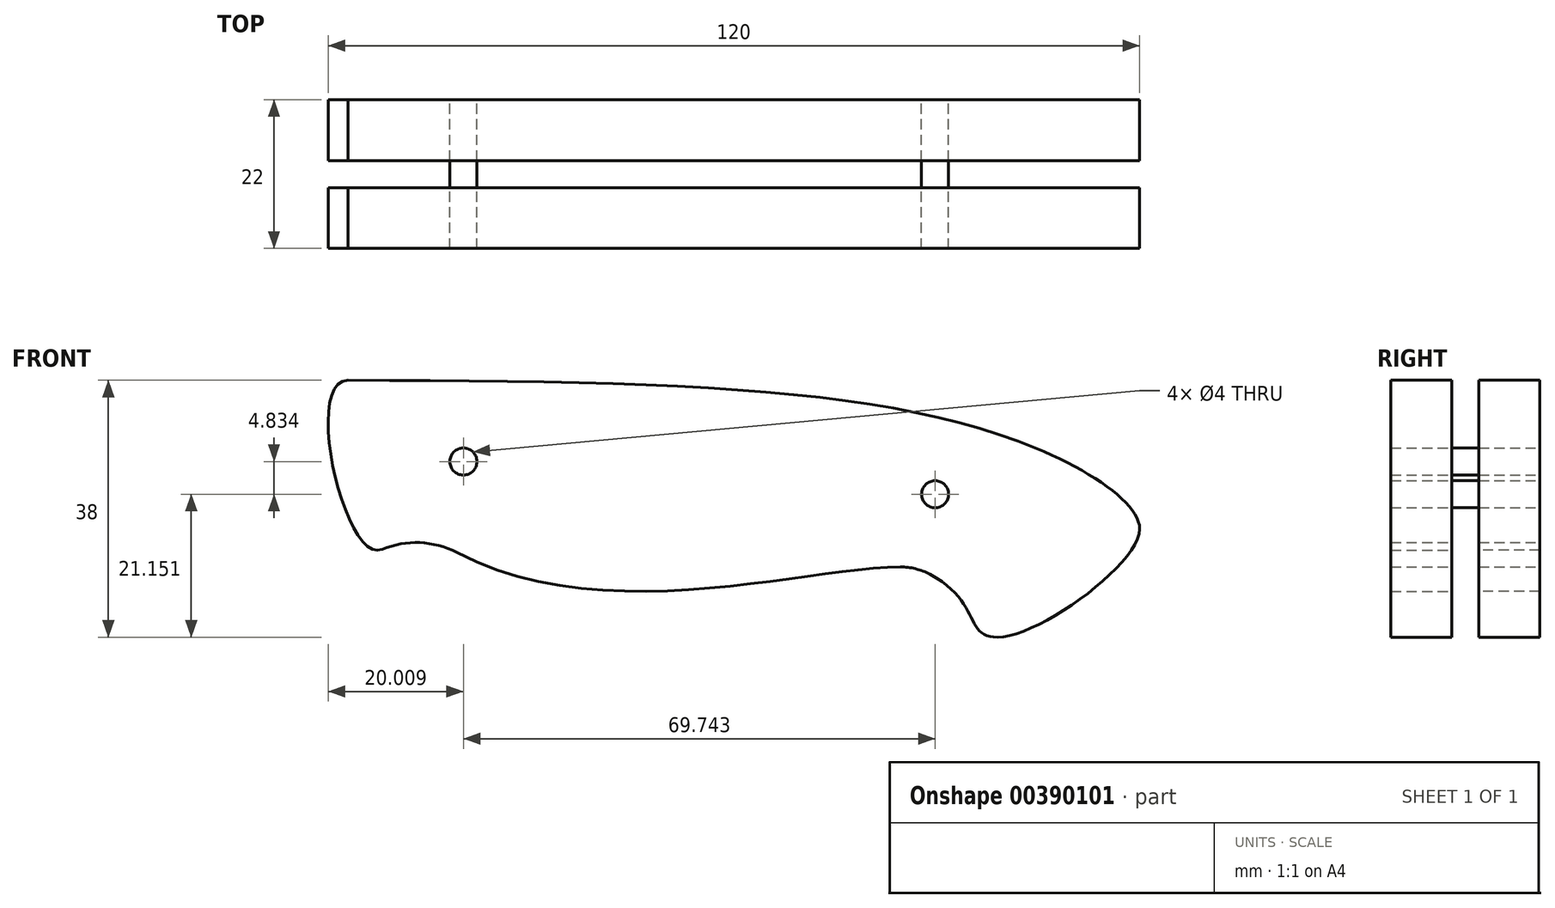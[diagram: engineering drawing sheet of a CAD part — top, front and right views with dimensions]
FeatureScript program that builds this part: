
annotation { "Feature Type Name" : "Feature", "Feature Type Description" : "" }
export const myFeature = defineFeature(function(context is Context, id is Id, definition is map)
    precondition{}
    {
        {
            var Q0;
            Q0=qCreatedBy(makeId("Front.planeOp"),FACE);
            var sketch = newSketch(context, id + "F0", { "sketchPlane" : qUnion([Q0])});
            skLineSegment(sketch, "E0.bottom", {"start": v(0, 0) * mm, "end": v(230, 0) * mm});
            skLineSegment(sketch, "E0.top", {"start": v(0, -38) * mm, "end": v(230, -38) * mm});
            skLineSegment(sketch, "E0.left", {"start": v(0, 0) * mm, "end": v(0, -38) * mm});
            skLineSegment(sketch, "E0.right", {"start": v(230, 0) * mm, "end": v(230, -38) * mm});
            skSolve(sketch);
        }
        {
            var Q0;
            Q0=makeQuery(id+"F0.imprint","IMPRINT",FACE,{"disambiguationData":[TD([[makeQuery(id+"F0.imprint","IMPRINT",EDGE,{"derivedFrom":sQuery(id+"F0.wireOp",EDGE,"E0.bottom")}),-1.0]])]});
            var sketch = newSketch(context, id + "F1", { "sketchPlane" : qUnion([Q0])});
            skLineSegment(sketch, "E1", {"start": v(0, 0) * mm, "end": v(0, -10) * mm, "construction": true});
            skLineSegment(sketch, "E2", {"start": v(110, 0) * mm, "end": v(230, 0) * mm, "construction": true});
            skLineSegment(sketch, "E3", {"start": v(110, 0) * mm, "end": v(110, -38) * mm, "construction": true});
            skFitSpline(sketch, "E4", {"points": [v(0, -10) * mm, v(110, -38) * mm], "startDerivative": vector(51, -84) * mm, "endDerivative": vector(120, 0) * mm});
            skFitSpline(sketch, "E5", {"points": [v(0, -10) * mm, v(110, 0) * mm], "startDerivative": vector(150, 30) * mm, "endDerivative": vector(210, 0) * mm});
            skLineSegment(sketch, "E6", {"start": v(110, -38) * mm, "end": v(70, -38) * mm, "construction": true});
            skLineSegment(sketch, "E7", {"start": v(110, 0) * mm, "end": v(40, 0) * mm, "construction": true});
            skLineSegment(sketch, "E8", {"start": v(110, 0) * mm, "end": v(0, 0) * mm, "construction": true});
            skLineSegment(sketch, "E9", {"start": v(110, -38) * mm, "end": v(123, -38) * mm, "construction": true});
            skLineSegment(sketch, "E10", {"start": v(123, -38) * mm, "end": v(123, -37) * mm, "construction": true});
            skArc(sketch, "E11", {"start": v(129, -25.47) * mm, "mid": v(116.25, -25.89) * mm, "end": v(110, -37) * mm});
            skFitSpline(sketch, "E12", {"points": [v(110, 0) * mm, v(212, -9) * mm, v(230, -22) * mm], "startDerivative": vector(219.85, 0) * mm, "endDerivative": vector(0, -37.77) * mm});
            skLineSegment(sketch, "E13", {"start": v(230, 0) * mm, "end": v(230, -22) * mm, "construction": true});
            skLineSegment(sketch, "E14", {"start": v(110, 0) * mm, "end": v(160, 0) * mm, "construction": true});
            skLineSegment(sketch, "E15", {"start": v(230, -22) * mm, "end": v(230, -18) * mm, "construction": true});
            skLineSegment(sketch, "E16", {"start": v(230, -38) * mm, "end": v(209, -38) * mm, "construction": true});
            skFitSpline(sketch, "E17", {"points": [v(230, -22) * mm, v(209, -38) * mm], "startDerivative": vector(0, -15.6) * mm, "endDerivative": vector(-18, 0) * mm});
            skLineSegment(sketch, "E18", {"start": v(230, -22) * mm, "end": v(230, -27.2) * mm, "construction": true});
            skLineSegment(sketch, "E19", {"start": v(209, -38) * mm, "end": v(215, -38) * mm, "construction": true});
            skLineSegment(sketch, "E20", {"start": v(129, -25.47) * mm, "end": v(151.18, -37) * mm, "construction": true});
            skArc(sketch, "E21", {"start": v(199, -28.7) * mm, "mid": v(196.87, -27.88) * mm, "end": v(194.6, -27.6) * mm});
            skLineSegment(sketch, "E22", {"start": v(194.6, -27.6) * mm, "end": v(180.6, -27.6) * mm, "construction": true});
            skFitSpline(sketch, "E23", {"points": [v(129, -25.47) * mm, v(194.6, -27.6) * mm], "startDerivative": vector(66.53, -34.62) * mm, "endDerivative": vector(42, 0) * mm});
            skLineSegment(sketch, "E24", {"start": v(204, -38) * mm, "end": v(209, -38) * mm, "construction": true});
            skLineSegment(sketch, "E25", {"start": v(194.6, -37) * mm, "end": v(204, -37) * mm, "construction": true});
            skLineSegment(sketch, "E26", {"start": v(199, -28.7) * mm, "end": v(206.6, -32.72) * mm, "construction": true});
            skFitSpline(sketch, "E27", {"points": [v(199, -28.7) * mm, v(209, -38) * mm], "startDerivative": vector(22.8, -12.08) * mm, "endDerivative": vector(15, 0) * mm});
            skLineSegment(sketch, "E28", {"start": v(209, -38) * mm, "end": v(204, -38) * mm, "construction": true});
            skLineSegment(sketch, "E29", {"start": v(0, -38) * mm, "end": v(17, -38) * mm, "construction": true});
            skLineSegment(sketch, "E30", {"start": v(0, 0) * mm, "end": v(50, 0) * mm});
            skLineSegment(sketch, "E31", {"start": v(110, -25.47) * mm, "end": v(129, -25.47) * mm, "construction": true});
            skLineSegment(sketch, "E32", {"start": v(194.6, -27.6) * mm, "end": v(230, -27.6) * mm, "construction": true});
            skLineSegment(sketch, "E33", {"start": v(204, -38) * mm, "end": v(204, -37) * mm, "construction": true});
            skLineSegment(sketch, "E34", {"start": v(110, -38) * mm, "end": v(106, -38) * mm, "construction": true});
            skLineSegment(sketch, "E35", {"start": v(106, -38) * mm, "end": v(106, -10) * mm, "construction": true});
            skLineSegment(sketch, "E36", {"start": v(106, -10) * mm, "end": v(96, -10) * mm, "construction": true});
            skLineSegment(sketch, "E37", {"start": v(96, -10) * mm, "end": v(96, -20) * mm, "construction": true});
            skArc(sketch, "E38", {"start": v(106, -20) * mm, "mid": v(103.07, -12.93) * mm, "end": v(96, -10) * mm});
            skPoint(sketch, "E39", {"position": v(106, -20) * mm});
            skLineSegment(sketch, "E40", {"start": v(106, -20) * mm, "end": v(106, -38) * mm});
            skLineSegment(sketch, "E41", {"start": v(110, 0) * mm, "end": v(113, 0) * mm, "construction": true});
            skLineSegment(sketch, "E42", {"start": v(118, -25) * mm, "end": v(112.46, -27.3) * mm, "construction": true});
            skLineSegment(sketch, "E43", {"start": v(118, -25) * mm, "end": v(110, -25) * mm, "construction": true});
            skFitSpline(sketch, "E44", {"points": [v(113, 0) * mm, v(118, -25) * mm], "startDerivative": vector(-20.6, 0) * mm, "endDerivative": vector(16.62, 6.92) * mm});
            skLineSegment(sketch, "E45", {"start": v(96, -10) * mm, "end": v(96, 0) * mm});
            skLineSegment(sketch, "E46", {"start": v(110, -37) * mm, "end": v(110, -38) * mm});
            skLineSegment(sketch, "E47", {"start": v(110, -9) * mm, "end": v(212, -9) * mm, "construction": true});
            skLineSegment(sketch, "E48", {"start": v(212, 0) * mm, "end": v(212, -9) * mm});
            skLineSegment(sketch, "E49", {"start": v(199, -28.7) * mm, "end": v(230, -28.7) * mm, "construction": true});
            skFitSpline(sketch, "E50", {"points": [v(208, -7.62) * mm, v(214, -36.61) * mm], "startDerivative": vector(40.02, -12.74) * mm, "endDerivative": vector(-21.9, -9.84) * mm, "construction": true});
            skLineSegment(sketch, "E51", {"start": v(208, -7.62) * mm, "end": v(221.34, -11.87) * mm, "construction": true});
            skLineSegment(sketch, "E52", {"start": v(214, -36.61) * mm, "end": v(221.3, -33.33) * mm, "construction": true});
            skLineSegment(sketch, "E53", {"start": v(208, -7.62) * mm, "end": v(230, -7.62) * mm, "construction": true});
            skLineSegment(sketch, "E54", {"start": v(214, -36.61) * mm, "end": v(230, -36.61) * mm, "construction": true});
            skSolve(sketch);
        }
        {
            var Q0;
            Q0=makeQuery(id+"F0.imprint","IMPRINT",FACE,{"disambiguationData":[TD([[makeQuery(id+"F0.imprint","IMPRINT",EDGE,{"derivedFrom":sQuery(id+"F0.wireOp",EDGE,"E0.bottom")}),-1.0]])]});
            var sketch = newSketch(context, id + "F2", { "sketchPlane" : qUnion([Q0])});
            skLineSegment(sketch, "E55", {"start": v(123, -24) * mm, "end": v(123, 0) * mm, "construction": true});
            skLineSegment(sketch, "E56", {"start": v(198.06, -28.26) * mm, "end": v(206.44, -7.14) * mm, "construction": true});
            skFitSpline(sketch, "E57", {"points": [v(123, -12) * mm, v(202.25, -17.7) * mm], "startDerivative": vector(111, 0) * mm, "endDerivative": vector(34.3, -13.6) * mm, "construction": true});
            skLineSegment(sketch, "E58", {"start": v(202.25, -17.7) * mm, "end": v(190.82, -13.17) * mm, "construction": true});
            skCircle(sketch, "E59", {"center": v(130, -12.01) * mm, "radius": 2 * mm});
            skCircle(sketch, "E60", {"center": v(199.75, -16.85) * mm, "radius": 2 * mm});
            skSolve(sketch);
        }
        {
            var Q0;
            {var subQ8=sQuery(id+"F1.wireOp",EDGE,"E5");Q0=makeQuery(id+"F1.imprint","IMPRINT",FACE,{"disambiguationData":[TD([[makeQuery(id+"F1.imprint","IMPRINT",EDGE,{"derivedFrom":subQ8}),-1.0]])]});}
            extrude(context, id + "F3", {"entities" : qUnion([Q0]), "endBound" : BoundingType.SYMMETRIC, "depth" : 4 * mm});
        }
        {
            var Q0;
            Q0=makeQuery(id+"F3.opExtrude","CAP_EDGE",EDGE,{"disambiguationData":[OSD([sQuery(id+"F1.wireOp",EDGE,"E4")])],"isStart":false});
            var Q1;
            Q1=makeQuery(id+"F3.opExtrude","CAP_EDGE",EDGE,{"disambiguationData":[OSD([sQuery(id+"F1.wireOp",EDGE,"E4")])],"isStart":true});
            chamfer(context, id + "F4", {"entities" : qUnion([Q0, Q1]), "chamferType" : ChamferType.TWO_OFFSETS, "width1" : 28 * mm, "oppositeDirection" : false, "width2" : 2 * mm, "tangentPropagation" : true});
        }
        {
            var Q0;
            {var subQ15=sQuery(id+"F1.wireOp",EDGE,"E38");Q0=makeQuery(id+"F1.imprint","IMPRINT",FACE,{"disambiguationData":[TD([[makeQuery(id+"F1.imprint","IMPRINT",EDGE,{"derivedFrom":subQ15}),-1.0]])]});}
            var Q1;
            Q1=makeQuery(id+"F1.imprint","IMPRINT",FACE,{"disambiguationData":[TD([[makeQuery(id+"F1.imprint","IMPRINT",EDGE,{"derivedFrom":sQuery(id+"F1.wireOp",EDGE,"E21")}),-1.0]])]});
            extrude(context, id + "F5", {"entities" : qUnion([Q0, Q1]), "operationType" : NewBodyOperationType.ADD, "endBound" : BoundingType.SYMMETRIC, "depth" : 4 * mm});
        }
        {
            var Q0;
            Q0=makeQuery(id+"F1.imprint","IMPRINT",FACE,{"disambiguationData":[TD([[makeQuery(id+"F1.imprint","IMPRINT",EDGE,{"derivedFrom":sQuery(id+"F1.wireOp",EDGE,"E21")}),-1.0]])]});
            extrude(context, id + "F6", {"entities" : qUnion([Q0]), "endBound" : BoundingType.SYMMETRIC, "depth" : 22 * mm});
        }
        {
            var Q0;
            Q0=qSketchRegion(id+"F0",true);
            extrude(context, id + "F7", {"entities" : qUnion([Q0]), "operationType" : NewBodyOperationType.REMOVE, "endBound" : BoundingType.SYMMETRIC, "depth" : 4 * mm});
        }
        {
            var Q0;
            Q0=makeQuery(id+"F2.imprint","IMPRINT",FACE,{"disambiguationData":[TD([[makeQuery(id+"F2.imprint","IMPRINT",EDGE,{"derivedFrom":sQuery(id+"F2.wireOp",EDGE,"E59")}),1.0]])]});
            var Q1;
            Q1=makeQuery(id+"F2.imprint","IMPRINT",FACE,{"disambiguationData":[TD([[makeQuery(id+"F2.imprint","IMPRINT",EDGE,{"derivedFrom":sQuery(id+"F2.wireOp",EDGE,"E60")}),1.0]])]});
            extrude(context, id + "F8", {"entities" : qUnion([Q0, Q1]), "endBound" : BoundingType.SYMMETRIC, "depth" : 22 * mm});
        }
        {
            var Q0;
            Q0=makeQuery(id+"F8.opExtrude","SWEPT_BODY",BODY,{"disambiguationData":[OSD([sQuery(id+"F2.wireOp",EDGE,"E59")])]});
            var Q1;
            Q1=makeQuery(id+"F8.opExtrude","SWEPT_BODY",BODY,{"disambiguationData":[OSD([sQuery(id+"F2.wireOp",EDGE,"E60")])]});
            var Q2;
            Q2=makeQuery(id+"F3.opExtrude","SWEPT_BODY",BODY,{"disambiguationData":[OSD([sQuery(id+"F1.wireOp",EDGE,"E4"),sQuery(id+"F1.wireOp",EDGE,"E5"),sQuery(id+"F1.wireOp",EDGE,"E38"),sQuery(id+"F1.wireOp",EDGE,"E40"),sQuery(id+"F1.wireOp",EDGE,"E45")])]});
            var Q3;
            Q3=makeQuery(id+"F7.boolean.opBoolean","SPLIT",BODY,{"disambiguationData":[OD(0.0)],"derivedFrom":makeQuery(id+"F6.opExtrude","SWEPT_BODY",BODY,{"disambiguationData":[OSD([sQuery(id+"F1.wireOp",EDGE,"E11"),sQuery(id+"F1.wireOp",EDGE,"E12"),sQuery(id+"F1.wireOp",EDGE,"E17"),sQuery(id+"F1.wireOp",EDGE,"E21"),sQuery(id+"F1.wireOp",EDGE,"E23"),sQuery(id+"F1.wireOp",EDGE,"E27"),sQuery(id+"F1.wireOp",EDGE,"E44")])]})});
            var Q4;
            Q4=makeQuery(id+"F7.boolean.opBoolean","SPLIT",BODY,{"disambiguationData":[OD(1.0)],"derivedFrom":makeQuery(id+"F6.opExtrude","SWEPT_BODY",BODY,{"disambiguationData":[OSD([sQuery(id+"F1.wireOp",EDGE,"E11"),sQuery(id+"F1.wireOp",EDGE,"E12"),sQuery(id+"F1.wireOp",EDGE,"E17"),sQuery(id+"F1.wireOp",EDGE,"E21"),sQuery(id+"F1.wireOp",EDGE,"E23"),sQuery(id+"F1.wireOp",EDGE,"E27"),sQuery(id+"F1.wireOp",EDGE,"E44")])]})});
            booleanBodies(context, id + "F9", {"operationType" : BooleanOperationType.SUBTRACTION, "tools" : qUnion([Q0, Q1]), "targets" : qUnion([Q2, Q3, Q4]), "keepTools" : true});
        }
    });
